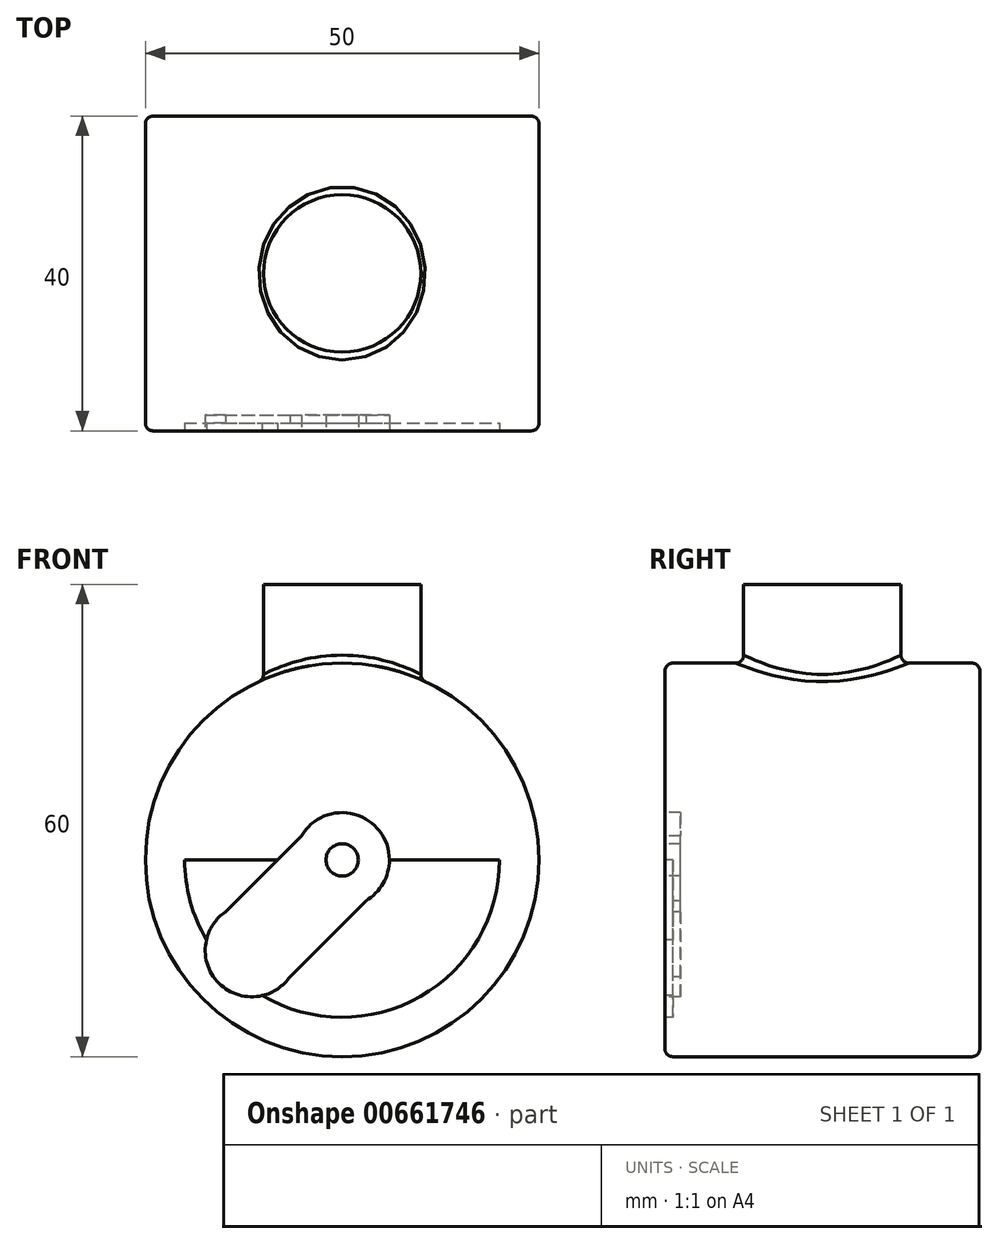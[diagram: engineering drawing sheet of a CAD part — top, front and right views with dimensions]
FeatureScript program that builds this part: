
annotation { "Feature Type Name" : "Feature", "Feature Type Description" : "" }
export const myFeature = defineFeature(function(context is Context, id is Id, definition is map)
    precondition{}
    {
        {
            var Q0;
            Q0=qCreatedBy(makeId("Front.planeOp"),FACE);
            var sketch = newSketch(context, id + "F0", { "sketchPlane" : qUnion([Q0])});
            skCircle(sketch, "E0", {"center": v(0, 0) * mm, "radius": 25 * mm});
            skLineSegment(sketch, "E1", {"start": v(0, 32.91) * mm, "end": v(-10, 32.91) * mm});
            skLineSegment(sketch, "E2", {"start": v(-10, 32.91) * mm, "end": v(-10, 22.91) * mm});
            skLineSegment(sketch, "E3", {"start": v(0, 32.91) * mm, "end": v(0, 0) * mm, "construction": true});
            skLineSegment(sketch, "E4.MirrorCS", {"start": v(10, 32.91) * mm, "end": v(10, 22.91) * mm});
            skLineSegment(sketch, "E5.MirrorCS", {"start": v(0, 32.91) * mm, "end": v(10, 32.91) * mm});
            skSolve(sketch);
        }
        {
            var Q0;
            {var subQ0=sQuery(id+"F0.wireOp",EDGE,"E0");var subQ1=makeQuery(id+"F0.imprint","INTERSECT",VERTEX,{"derivedFrom":[subQ0,sQuery(id+"F0.wireOp",EDGE,"E2")]});Q0=makeQuery(id+"F0.imprint","IMPRINT",FACE,{"disambiguationData":[TD([[makeQuery(id+"F0.imprint","IMPRINT",EDGE,{"disambiguationData":[TD([[subQ1,1.0]])],"derivedFrom":subQ0}),1.0]])]});}
            extrude(context, id + "F1", {"entities" : qUnion([Q0]), "endBound" : BoundingType.SYMMETRIC, "depth" : 40 * mm, "offsetDistance" : 25 * mm});
        }
        {
            var Q0;
            Q0=makeQuery(id+"F0.imprint","IMPRINT",FACE,{"disambiguationData":[TD([[makeQuery(id+"F0.imprint","IMPRINT",EDGE,{"derivedFrom":sQuery(id+"F0.wireOp",EDGE,"E1")}),1.0]])]});
            extrude(context, id + "F2", {"entities" : qUnion([Q0]), "endBound" : BoundingType.SYMMETRIC, "depth" : 10 * mm, "offsetDistance" : 25 * mm});
        }
        {
            var Q0;
            Q0=makeQuery(id+"F2.opExtrude","SWEPT_BODY",BODY,{"disambiguationData":[OSD([sQuery(id+"F0.wireOp",EDGE,"E0"),sQuery(id+"F0.wireOp",EDGE,"E1"),sQuery(id+"F0.wireOp",EDGE,"E2"),sQuery(id+"F0.wireOp",EDGE,"E4.MirrorCS"),sQuery(id+"F0.wireOp",EDGE,"E5.MirrorCS")])]});
            deleteBodies(context, id + "F3", {"entities" : qUnion([Q0])});
        }
        {
            var Q0;
            Q0=qCreatedBy(makeId("Top.planeOp"),FACE);
            var sketch = newSketch(context, id + "F4", { "sketchPlane" : qUnion([Q0])});
            skCircle(sketch, "E6", {"center": v(0, 0) * mm, "radius": 10 * mm});
            skSolve(sketch);
        }
        {
            var Q0;
            Q0=makeQuery(id+"F4.imprint","IMPRINT",FACE,{"disambiguationData":[TD([[makeQuery(id+"F4.imprint","IMPRINT",EDGE,{"derivedFrom":sQuery(id+"F4.wireOp",EDGE,"E6")}),1.0]])]});
            extrude(context, id + "F5", {"entities" : qUnion([Q0]), "operationType" : NewBodyOperationType.ADD, "depth" : 35 * mm, "offsetDistance" : 25 * mm});
        }
        {
            var Q0;
            Q0=makeQuery(id+"F1.opExtrude","SWEPT_FACE",FACE,{"disambiguationData":[OSD([sQuery(id+"F0.wireOp",EDGE,"E0")])]});
            fillet(context, id + "F6", {"entities" : qUnion([Q0]), "radius" : 1 * mm, "tangentPropagation" : true, "allowEdgeOverflow" : false});
        }
        {
            var Q0;
            Q0=makeQuery(id+"F1.opExtrude","CAP_FACE",FACE,{"disambiguationData":[OSD([sQuery(id+"F0.wireOp",EDGE,"E0")])],"isStart":false});
            var sketch = newSketch(context, id + "F7", { "sketchPlane" : qUnion([Q0])});
            skLineSegment(sketch, "E7", {"start": v(-24, 0) * mm, "end": v(24, 0) * mm, "construction": true});
            skLineSegment(sketch, "E8", {"start": v(0, 24) * mm, "end": v(0, -24) * mm, "construction": true});
            skArc(sketch, "E9", {"start": v(-20, 0) * mm, "mid": v(-19.3, -5.26) * mm, "end": v(-17.24, -10.15) * mm});
            skLineSegment(sketch, "E10", {"start": v(-20, 0) * mm, "end": v(20, 0) * mm});
            skArc(sketch, "E11", {"start": v(3.02, -5.18) * mm, "mid": v(5.63, 2.09) * mm, "end": v(-1.1, 5.9) * mm});
            skLineSegment(sketch, "E12", {"start": v(0, 0) * mm, "end": v(-16.25, 0) * mm, "construction": true});
            skCircle(sketch, "E13", {"center": v(0, 0) * mm, "radius": 2.05 * mm});
            skArc(sketch, "E14", {"start": v(-14.84, -6.63) * mm, "mid": v(-15.66, -15.66) * mm, "end": v(-6.63, -14.84) * mm});
            skLineSegment(sketch, "E15", {"start": v(-14.84, -6.63) * mm, "end": v(-5.18, 3.02) * mm});
            skLineSegment(sketch, "E16.MirrorCS", {"start": v(-6.63, -14.84) * mm, "end": v(3.02, -5.18) * mm});
            skArc(sketch, "E17.trimOffspring", {"start": v(3.02, -5.18) * mm, "mid": v(4.24, 4.24) * mm, "end": v(-5.18, 3.02) * mm});
            skArc(sketch, "E18.trimOffspring", {"start": v(-10.15, -17.24) * mm, "mid": v(9.93, -17.36) * mm, "end": v(20, 0) * mm});
            skSolve(sketch);
        }
        {
            var Q0;
            {var subQ1=sQuery(id+"F7.wireOp",EDGE,"E16.MirrorCS");Q0=makeQuery(id+"F7.imprint","IMPRINT",FACE,{"disambiguationData":[TD([[makeQuery(id+"F7.imprint","IMPRINT",EDGE,{"derivedFrom":subQ1}),-1.0]])]});}
            var Q1;
            {var subQ0=sQuery(id+"F7.wireOp",EDGE,"E9");Q1=makeQuery(id+"F7.imprint","IMPRINT",FACE,{"disambiguationData":[TD([[makeQuery(id+"F7.imprint","IMPRINT",EDGE,{"derivedFrom":subQ0}),1.0]])]});}
            extrude(context, id + "F8", {"entities" : qUnion([Q0, Q1]), "operationType" : NewBodyOperationType.REMOVE, "oppositeDirection" : true, "depth" : 1 * mm, "offsetDistance" : 25 * mm});
        }
        {
            var Q0;
            {var subQ11=sQuery(id+"F7.wireOp",EDGE,"E16.MirrorCS");Q0=makeQuery(id+"F7.imprint","IMPRINT",FACE,{"disambiguationData":[TD([[makeQuery(id+"F7.imprint","IMPRINT",EDGE,{"derivedFrom":subQ11}),1.0]])]});}
            var Q1;
            {var subQ4=sQuery(id+"F7.wireOp",EDGE,"E17.trimOffspring");var subQ6=makeQuery(id+"F7.imprint","IMPRINT",VERTEX,{"derivedFrom":subQ4});Q1=makeQuery(id+"F7.imprint","IMPRINT",FACE,{"disambiguationData":[TD([[makeQuery(id+"F7.imprint","IMPRINT",EDGE,{"disambiguationData":[TD([[subQ6,1.0]])],"derivedFrom":subQ4}),1.0]])]});}
            extrude(context, id + "F9", {"entities" : qUnion([Q0, Q1]), "operationType" : NewBodyOperationType.REMOVE, "oppositeDirection" : true, "depth" : 2 * mm, "offsetDistance" : 25 * mm});
        }
    });
